# Revit family: Pot_Filler-DXV-Traditional-D35402900_Series
name_source: partatom
category: Plumbing Fixtures
revit_build: Autodesk Revit 2014 (Build: 20130308_1515(x64)
units: mm (PartAtom-declared; Revit-internal decimal feet)

## types (2) — shared parameters
Assembly Code = D2020300
CW Connection = Yes
CWFU = 3
Cold Water Connection Diameter = 1/2"
Cold Water Connection Radius = 1/4"
Default Elevation = 40"
Description = Traditional Pot Filler
Flow Rate = 3.0 GPM (11.4L/min)
HW Connection = No
Height = 6 3/4"
Installation Type = Wall Mounted
Length = 4 1/2"
Manufacturer = DVX
Price = Prices may vary. Please consult Manufacturer Representative for most up-to-date price list.
Product Documentation Link = https://dxv01.blob.core.windows.net
Product Page URL = https://www.dxv.com
URL = http://www.dxv.com
Vent Connection = No
Warranty Documentation Link = https://www.dxv.com
Waste Connection = No
Width = 15 7/8"
zero-valued in all types: HWFU, WFU

## per-type parameters (varying)
| type | Finish | Material |
| D35402900.355 | Metal-DXV-355-Ultra Steel | Metal-DXV-355-Ultra Steel |
| D35402900.100 | Metal-DXV-100-Polished Chrome | Metal-DXV-100-Polished Chrome |

note: column(s) folded — value = type name in every type: Model

## geometry (parser evidence)
native form markers: Sweep x1
no freeform markers — native parametric forms only
